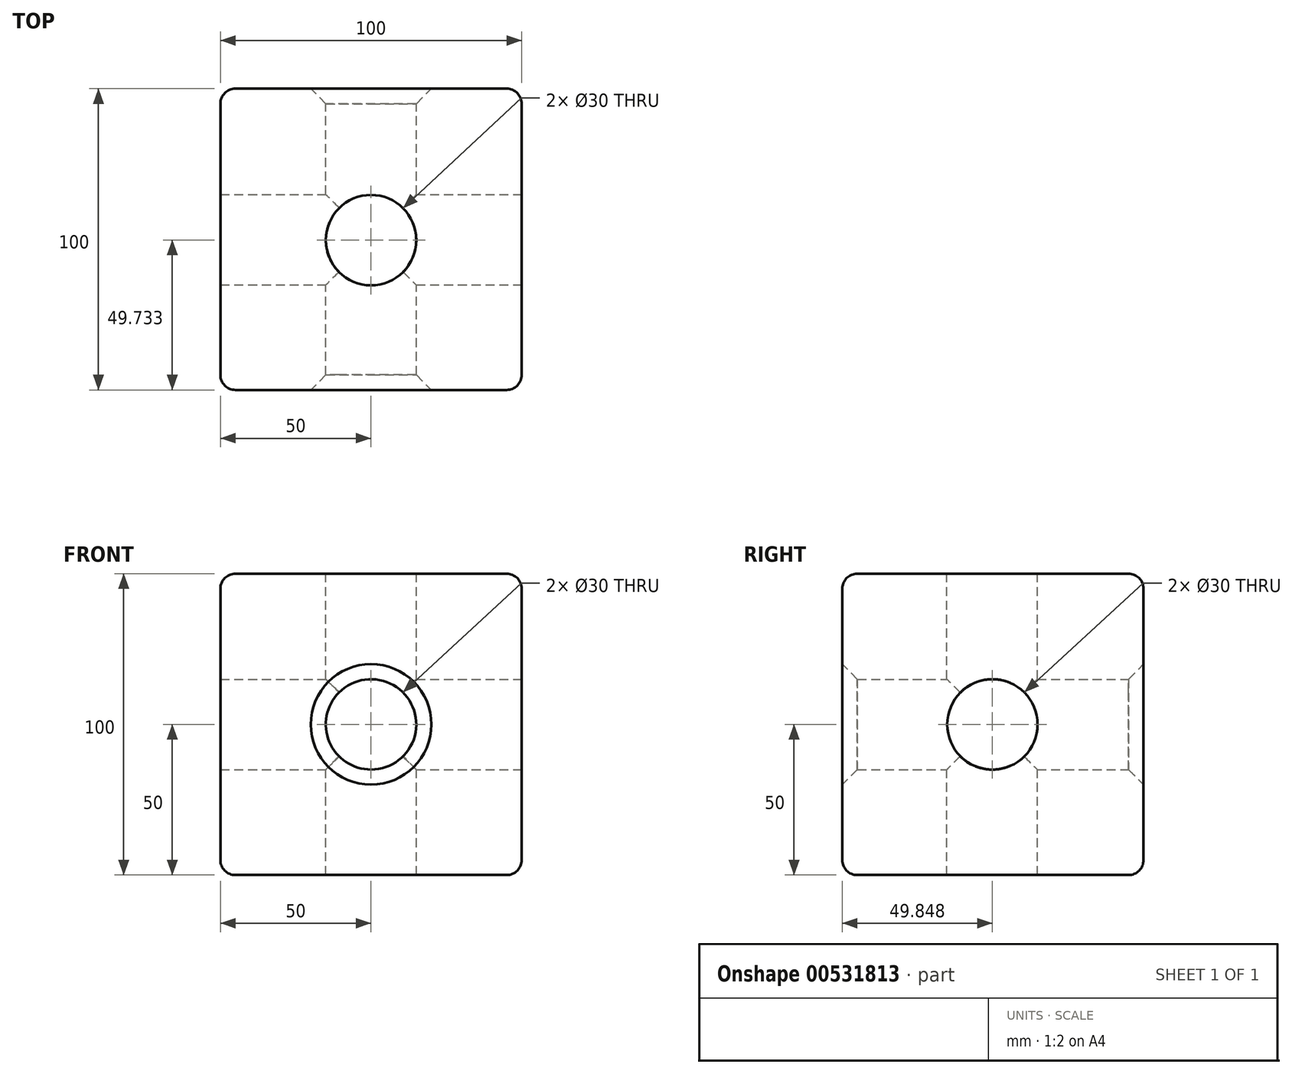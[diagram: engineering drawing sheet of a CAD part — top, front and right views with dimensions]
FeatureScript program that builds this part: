
annotation { "Feature Type Name" : "Feature", "Feature Type Description" : "" }
export const myFeature = defineFeature(function(context is Context, id is Id, definition is map)
    precondition{}
    {
        {
            var Q0;
            Q0=qCreatedBy(makeId("Front.planeOp"),FACE);
            var sketch = newSketch(context, id + "F0", { "sketchPlane" : qUnion([Q0])});
            skLineSegment(sketch, "E0.bottom", {"start": v(50, 50) * mm, "end": v(-50, 50) * mm});
            skLineSegment(sketch, "E0.top", {"start": v(50, -50) * mm, "end": v(-50, -50) * mm});
            skLineSegment(sketch, "E0.left", {"start": v(50, 50) * mm, "end": v(50, -50) * mm});
            skLineSegment(sketch, "E0.right", {"start": v(-50, 50) * mm, "end": v(-50, -50) * mm});
            skPoint(sketch, "E0.middle", {"position": v(0, 0) * mm});
            skCircle(sketch, "E1", {"center": v(0, 0) * mm, "radius": 15 * mm});
            skSolve(sketch);
        }
        {
            var Q0;
            Q0=makeQuery(id+"F0.imprint","IMPRINT",FACE,{"disambiguationData":[TD([[makeQuery(id+"F0.imprint","IMPRINT",EDGE,{"derivedFrom":sQuery(id+"F0.wireOp",EDGE,"E0.bottom")}),1.0]])]});
            extrude(context, id + "F1", {"entities" : qUnion([Q0]), "depth" : 100 * mm, "offsetDistance" : 25 * mm});
        }
        {
            var Q0;
            Q0=makeQuery(id+"F1.opExtrude","SWEPT_FACE",FACE,{"disambiguationData":[OSD([sQuery(id+"F0.wireOp",EDGE,"E0.left")])]});
            var sketch = newSketch(context, id + "F2", { "sketchPlane" : qUnion([Q0])});
            skCircle(sketch, "E2", {"center": v(-50.15, 0) * mm, "radius": 15 * mm});
            skPoint(sketch, "E2.centerSnap0", {"position": v(0, 0) * mm});
            skSolve(sketch);
        }
        {
            var Q0;
            Q0 = qSketchRegion(id + "F2", true);
            extrude(context, id + "F3", {"entities" : qUnion([Q0]), "operationType" : NewBodyOperationType.REMOVE, "oppositeDirection" : true, "depth" : 100 * mm, "offsetDistance" : 25 * mm});
        }
        {
            var Q0;
            Q0=makeQuery(id+"F1.opExtrude","SWEPT_FACE",FACE,{"disambiguationData":[OSD([sQuery(id+"F0.wireOp",EDGE,"E0.bottom")])]});
            var sketch = newSketch(context, id + "F4", { "sketchPlane" : qUnion([Q0])});
            skCircle(sketch, "E3", {"center": v(0, -50.27) * mm, "radius": 15 * mm});
            skSolve(sketch);
        }
        {
            var Q0;
            Q0 = qSketchRegion(id + "F4", true);
            extrude(context, id + "F5", {"entities" : qUnion([Q0]), "operationType" : NewBodyOperationType.REMOVE, "oppositeDirection" : true, "depth" : 100 * mm, "offsetDistance" : 25 * mm});
        }
        {
            var Q0;
            Q0=makeQuery(id+"F1.opExtrude","CAP_EDGE",EDGE,{"disambiguationData":[OSD([sQuery(id+"F0.wireOp",EDGE,"E0.bottom")])],"isStart":false});
            var Q1;
            Q1=makeQuery(id+"F1.opExtrude","SWEPT_EDGE",EDGE,{"disambiguationData":[OSD([sQuery(id+"F0.wireOp",EDGE,"E0.bottom"),sQuery(id+"F0.wireOp",EDGE,"E0.left")])]});
            var Q2;
            Q2=makeQuery(id+"F1.opExtrude","CAP_EDGE",EDGE,{"disambiguationData":[OSD([sQuery(id+"F0.wireOp",EDGE,"E0.left")])],"isStart":false});
            var Q3;
            Q3=makeQuery(id+"F1.opExtrude","CAP_EDGE",EDGE,{"disambiguationData":[OSD([sQuery(id+"F0.wireOp",EDGE,"E0.top")])],"isStart":false});
            var Q4;
            Q4=makeQuery(id+"F1.opExtrude","SWEPT_EDGE",EDGE,{"disambiguationData":[OSD([sQuery(id+"F0.wireOp",EDGE,"E0.top"),sQuery(id+"F0.wireOp",EDGE,"E0.left")])]});
            var Q5;
            Q5=makeQuery(id+"F1.opExtrude","CAP_EDGE",EDGE,{"disambiguationData":[OSD([sQuery(id+"F0.wireOp",EDGE,"E0.left")])],"isStart":true});
            var Q6;
            Q6=makeQuery(id+"F1.opExtrude","CAP_EDGE",EDGE,{"disambiguationData":[OSD([sQuery(id+"F0.wireOp",EDGE,"E0.bottom")])],"isStart":true});
            var Q7;
            Q7=makeQuery(id+"F1.opExtrude","CAP_EDGE",EDGE,{"disambiguationData":[OSD([sQuery(id+"F0.wireOp",EDGE,"E0.right")])],"isStart":true});
            var Q8;
            Q8=makeQuery(id+"F1.opExtrude","CAP_EDGE",EDGE,{"disambiguationData":[OSD([sQuery(id+"F0.wireOp",EDGE,"E0.top")])],"isStart":true});
            var Q9;
            Q9=makeQuery(id+"F1.opExtrude","SWEPT_EDGE",EDGE,{"disambiguationData":[OSD([sQuery(id+"F0.wireOp",EDGE,"E0.top"),sQuery(id+"F0.wireOp",EDGE,"E0.right")])]});
            var Q10;
            Q10=makeQuery(id+"F1.opExtrude","SWEPT_EDGE",EDGE,{"disambiguationData":[OSD([sQuery(id+"F0.wireOp",EDGE,"E0.bottom"),sQuery(id+"F0.wireOp",EDGE,"E0.right")])]});
            var Q11;
            Q11=makeQuery(id+"F1.opExtrude","CAP_EDGE",EDGE,{"disambiguationData":[OSD([sQuery(id+"F0.wireOp",EDGE,"E0.right")])],"isStart":false});
            fillet(context, id + "F6", {"entities" : qUnion([Q0, Q1, Q2, Q3, Q4, Q5, Q6, Q7, Q8, Q9, Q10, Q11]), "radius" : 5 * mm, "tangentPropagation" : true, "allowEdgeOverflow" : false});
        }
        {
            var Q0;
            Q0=makeQuery(id+"F1.opExtrude","CAP_EDGE",EDGE,{"disambiguationData":[OSD([sQuery(id+"F0.wireOp",EDGE,"E1")])],"isStart":false});
            var Q1;
            Q1=makeQuery(id+"F5.boolean.opBoolean","COPY",EDGE,{"derivedFrom":makeQuery(id+"F5.opExtrude","CAP_EDGE",EDGE,{"disambiguationData":[OSD([sQuery(id+"F4.wireOp",EDGE,"E3")])],"isStart":true})});
            var Q2;
            Q2=makeQuery(id+"F3.boolean.opBoolean","COPY",EDGE,{"derivedFrom":makeQuery(id+"F3.opExtrude","CAP_EDGE",EDGE,{"disambiguationData":[OSD([sQuery(id+"F2.wireOp",EDGE,"E2")])],"isStart":true})});
            var Q3;
            Q3=makeQuery(id+"F1.opExtrude","CAP_EDGE",EDGE,{"disambiguationData":[OSD([sQuery(id+"F0.wireOp",EDGE,"E1")])],"isStart":true});
            var Q4;
            Q4=makeQuery(id+"F5.boolean.opBoolean","COPY",EDGE,{"derivedFrom":makeQuery(id+"F5.opExtrude","CAP_EDGE",EDGE,{"disambiguationData":[OSD([sQuery(id+"F4.wireOp",EDGE,"E3")])],"isStart":false})});
            var Q5;
            Q5=makeQuery(id+"F3.boolean.opBoolean","COPY",EDGE,{"derivedFrom":makeQuery(id+"F3.opExtrude","CAP_EDGE",EDGE,{"disambiguationData":[OSD([sQuery(id+"F2.wireOp",EDGE,"E2")])],"isStart":false})});
            chamfer(context, id + "F7", {"entities" : qUnion([Q0, Q1, Q2, Q3, Q4, Q5]), "width" : 5 * mm, "tangentPropagation" : true});
        }
    });
